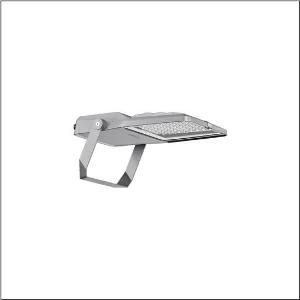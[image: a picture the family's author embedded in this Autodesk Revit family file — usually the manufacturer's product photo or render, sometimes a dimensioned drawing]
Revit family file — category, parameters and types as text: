
# Revit family: floodlight_fl_21_iq_mini___pl52_5xa7772c3d1a_c98d
name_source: partatom
category: Lighting Fixtures
units: mm (PartAtom-declared; Revit-internal decimal feet)

## family parameters
Cut with Voids When Loaded = No
Host = Face
Light Source = No
Part Type = Normal
Room Calculation Point = No
Round Connector Dimension = Use Diameter
Shared = No

## types (1)
- --- (1 x LED, 10510 lm, 87.2 W, 3000K)
    Apparent Load = 87 VA
    CIE Flux Codes = 26 60 98 100 100
    Color Rendering = 80
    Color Temperature = 3000K
    Default Elevation = 1800 mm
    Description = Floodlight FL 21 iQ mini, floodlight, primary light control with lens, of PMMA, primary optical cover: protective disc, of toughened safety glass, transparent, light distribution: PL52, light emission: direct distribution, installation type: surface-mounted, LED, High Power LED, rated luminous flux: 10.510lm, luminous efficacy: 121lm/W, light colour: 830, colour temperature: 3000K, control: Street-Remote, Auto-Match, Temp-Guard, Night-Set, Smart-Wire, Desk-Remote (wireless, voltage-free reading and setting of iQ features in the workshop via application-optimized NFC function/RFID function), optimised constant luminous flux control (CLO 2.0), with terminal, 6-pole, mains connection: 220..240V, AC, 50/60Hz, start of lifetime: 87W, end of service life: 92W, reduction: 40W, luminaire housing, of diecast aluminium, powder-coated, Siteco® metallic grey (DB 702S), corrosivity category C5 mid according to DIN EN ISO 12944, sealing non-destructively replaceable, mounting bracket, of steel, galvanised, powder-coated, Siteco® metallic grey (DB 702S), protection rating (complete): IP66, insulation class (complete): insulation class II (safety insulation), certification: CE, ENEC, VDE, protection symbol: D, impact resistance: IK08, permissible operating ambient temperature: -40..+40°C, permissible operating ambient temperature for outdoor applications: -40..+50°C, standard: DIN EN 12944, LABS conformity tested according to VDMA 24364:2018-05, packaging unit: 1 piece

Light Distribution: PL52
    Height = 70 mm
    Lamp = 1 x LED
    Lamp Light Flux = 10510 lm
    Lamp Power = 87.2 W
    Lamp count = 1
    Length = 485 mm
    Luminous efficacy = 121 lm/W
    Manufacturer = Siteco
    ModVariant = No
    Model = 5XA7772C3D1A
    Number of Poles = 1
    OnlyDefault = Yes
    Power Factor = 1
    Product Name = Floodlight FL 21 iQ mini | PL52
    Product group = floodlight | pylon annexe
    ProductGroupID = 6200
    Protection Class = Protection class II
    Protection Degree = IP 66
    RLX_Detail_Level = 1
    RLX_Emergency_Light_Flux = 0 lm
    RLX_Emergency_Type = 0
    RLX_Emergency_Type_DB = No
    RlxData = <blob elided: 96373 chars, md5=41dff3cb>
    Socket = socket
    Standby Power = 0 W
    System Light Flux = 10510 lm
    System Power = 87 W
    Type Comments = factory setting: luminous flux: 100 % | dim-lin: 254 | 456 mA
    Type Image = l_1006845.jpg
    URL = http://relux.com
    VarID = @adj_114419
    Voltage = 0 V
    Weight = 0.00 kg
    Width = 337 mm

## geometry (parser evidence)
native form markers: Blend x4, Sweep x13
no freeform markers — native parametric forms only
